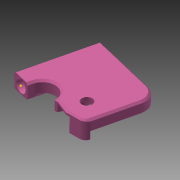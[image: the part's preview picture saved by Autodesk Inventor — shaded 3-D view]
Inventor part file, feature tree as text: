
AUTODESK INVENTOR PART (.ipt)
format: ipt  version: 2014 (Build 180170000, 170)  size: 430,080 bytes
history: native  units: mm
features: sketch x13, extrude x11, other x10, fillet x4, chamfer x3, plane x2, projected_geometry x2, draft x1, thicken_offset x1
ambient origin geometry x8: Origin, YZ Plane, XZ Plane, XY Plane, X Axis, Y Axis, Z Axis, Center Point
bodies: Solid1 (feature_tree)
feature tree (47):
  sketch  "Sketch1"  dims[d0=7.7mm d1=3.0mm]
  extrude  "Extrusion1"  Depth=3.0mm
  extrude  "Extrusion2"  Depth=1.5mm
  sketch  "Sketch3"  dims[d4=11.0mm d5=11.0mm]
  extrude  "Extrusion3"  Depth=11.0mm
  extrude  "Extrusion4"  Depth=20.0mm
  other  "UCS1"
  extrude  "Extrusion5"  Depth=35.0mm
  extrude  "Extrusion10"  Depth=14.0mm
  extrude  "Extrusion6"  Depth=8.0mm
  extrude  "Extrusion7"  Depth=3.0mm
  fillet  "Fillet2"  Radius=2.0mm
  fillet  "Fillet1"  Radius=5.8mm
  extrude  "Extrusion8"  TaperAngle=0.0deg  [1 undecoded]
  extrude  "Extrusion9"  Depth=2.0mm TaperAngle=0.0deg
  plane  "Work Plane1"
  extrude  "Extrusion11"  Depth=10.0mm TaperAngle=0.0deg
  fillet  "Fillet3"  Radius=10.0mm
  chamfer  "Chamfer1"  Distance=8.0mm
  chamfer  "Chamfer2"  Distance=4.0mm
  chamfer  "Chamfer3"  Distance=3.0mm
  plane  "Work Plane2"
  sketch  "Sketch14"  dims[d41=1.0mm d42=8.0mm d43=4.0mm d44=3.0mm d45=11.5mm d46=7.029049mm d47=4.0mm d48=0.0mm d49=3.0mm d50=1.0mm d51=0.5mm d52=2.0mm d53=45.0deg d54=1.0mm d55=2.0mm d56=45.0deg d57=2.5mm d58=0.0mm d59=0.0mm d60=0.0mm d64=-3.5mm d65=3.535mm d66=3.0mm d67=0.0mm d68=0.5mm d69=2.0mm d70=45.0deg d71=4.0mm d72=4.0mm d73=1.0mm d74=0.436332mm d75=0.2mm d76=0.2mm]
  fillet  "Fillet4"  Radius=11.5mm
  draft  "FaceDraft1"
  thicken_offset  "Thicken1"
  sketch  "Sketch2"  dims[d2=18.5mm d3=1.5mm]
  sketch  "Sketch4"  dims[d6=26.703538mm d7=20.0mm]
  sketch  "Sketch5"  dims[d8=40.0mm d9=35.0mm]
  sketch  "Sketch6"  dims[d10=4.0mm d11=0.0mm d12=14.0mm]
  projected_geometry  "Projected Loop1"
  sketch  "Sketch7"  dims[d13=19.5mm d14=8.0mm]
  sketch  "Sketch8"  dims[d15=0.0mm d16=0.0mm d17=3.0mm]
  sketch  "Sketch9"  dims[d18=0.0mm d19=0.0mm d20=0.0mm d21=0.0mm d22=0.0mm d23=0.0mm d24=2.0mm d25=0.0mm d26=5.8mm]
  sketch  "Sketch10"  dims[d27=2.0mm d28=0.0mm d29=0.0mm d30=0.0mm]
  sketch  "Sketch11"  dims[d32=16.0mm d33=2.0mm d34=0.0mm]
  sketch  "Sketch13"  dims[d35=6.85mm d37=1.5mm d38=0.0mm d39=10.0mm]
  other  "Work Axis1"
  other  "Work Point1"
  other  "UCS1: YZ Plane"
  other  "UCS1: XZ Plane"
  other  "UCS1: XY Plane"
  other  "UCS1: X Axis"
  other  "UCS1: Y Axis"
  other  "UCS1: Z Axis"
  other  "UCS1: Center Point"
  projected_geometry  "Project Cut Edges1"
note: 1 required parameter value undecoded (feature->parameter linkage not recoverable at this tier; creation-order binding heuristic only, values carry confidence <= 0.55)
